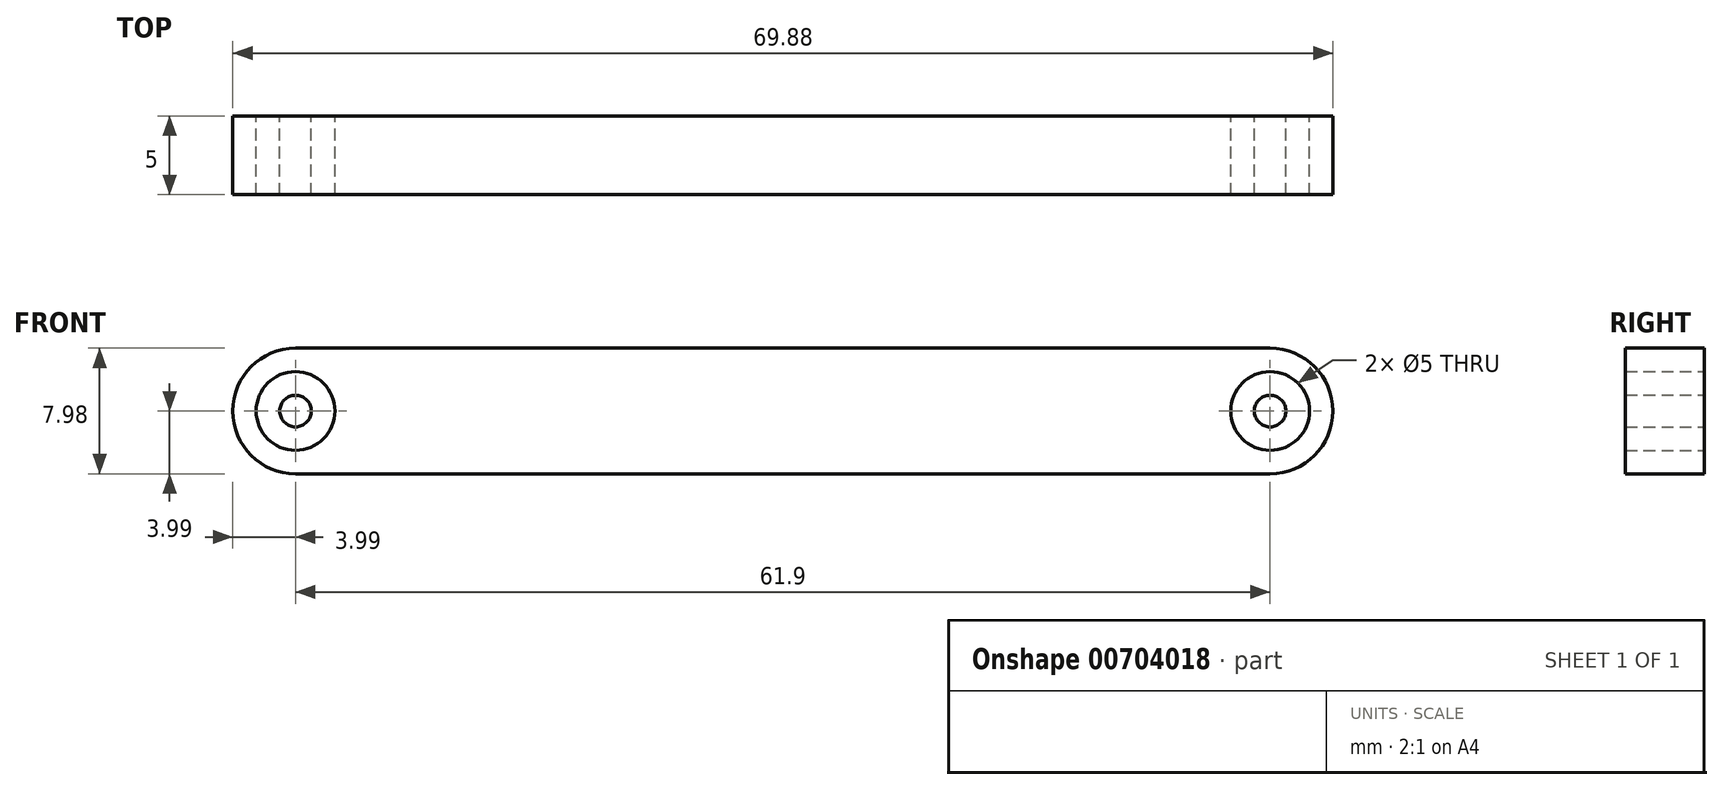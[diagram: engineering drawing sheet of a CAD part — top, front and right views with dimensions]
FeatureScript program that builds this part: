
annotation { "Feature Type Name" : "Feature", "Feature Type Description" : "" }
export const myFeature = defineFeature(function(context is Context, id is Id, definition is map)
    precondition{}
    {
        {
            var Q0;
            Q0=qCreatedBy(makeId("Front.planeOp"),FACE);
            var sketch = newSketch(context, id + "F0", { "sketchPlane" : qUnion([Q0])});
            skCircle(sketch, "E0", {"center": v(0, 0) * mm, "radius": 2.5 * mm});
            skCircle(sketch, "E1", {"center": v(0, 0) * mm, "radius": 1 * mm});
            skArc(sketch, "E2", {"start": v(0, -3.99) * mm, "mid": v(-3.99, 0) * mm, "end": v(0, 3.99) * mm});
            skCircle(sketch, "E3", {"center": v(61.9, 0) * mm, "radius": 2.5 * mm});
            skCircle(sketch, "E4", {"center": v(61.9, 0) * mm, "radius": 1 * mm});
            skArc(sketch, "E5", {"start": v(61.9, -3.99) * mm, "mid": v(65.89, 0) * mm, "end": v(61.9, 3.99) * mm});
            skLineSegment(sketch, "E6", {"start": v(0, 3.99) * mm, "end": v(61.9, 3.99) * mm});
            skLineSegment(sketch, "E7", {"start": v(0, -3.99) * mm, "end": v(61.9, -3.99) * mm});
            skSolve(sketch);
        }
        {
            var Q0;
            Q0=makeQuery(id+"F0.imprint","IMPRINT",FACE,{"disambiguationData":[TD([[makeQuery(id+"F0.imprint","IMPRINT",EDGE,{"derivedFrom":sQuery(id+"F0.wireOp",EDGE,"E0")}),-1.0]])]});
            var Q1;
            Q1=makeQuery(id+"F0.imprint","IMPRINT",FACE,{"disambiguationData":[TD([[makeQuery(id+"F0.imprint","IMPRINT",EDGE,{"derivedFrom":sQuery(id+"F0.wireOp",EDGE,"E1")}),1.0]])]});
            var Q2;
            Q2=makeQuery(id+"F0.imprint","IMPRINT",FACE,{"disambiguationData":[TD([[makeQuery(id+"F0.imprint","IMPRINT",EDGE,{"derivedFrom":sQuery(id+"F0.wireOp",EDGE,"E4")}),1.0]])]});
            extrude(context, id + "F1", {"entities" : qUnion([Q0, Q1, Q2]), "depth" : 5 * mm, "offsetDistance" : 25.4 * mm});
        }
    });
